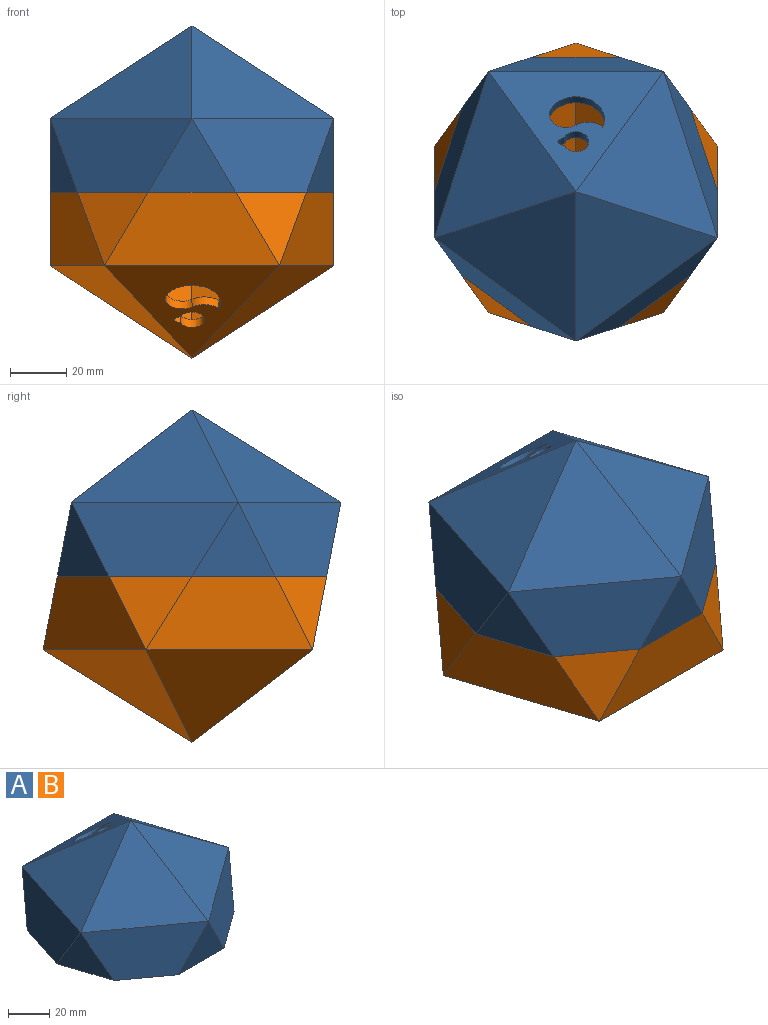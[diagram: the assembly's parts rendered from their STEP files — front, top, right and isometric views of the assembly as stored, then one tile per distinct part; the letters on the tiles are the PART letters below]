
ASSEMBLY  parts=2 mates=1
PART A: 43 faces, bbox 101.1x101.2x59.3 mm
  f0: plane 57.87x24.45mm, normal (0,-0.98,-0.19), area 1027.3mm2, adj f2,f20,f21,f26,f34,f35,f36
  f1: plane 28.74x24.45mm, normal (0,0.98,0.19), area 302.3mm2, adj f2,f24,f25,f31,f32,f33
  f2: plane 101.13x96.18mm, normal (0,0,-1), area 1072.3mm2, adj f0,f1,f3,f4,f5,f6,f7,f8
  f3: plane 29.53x26.42mm, normal (-0.93,-0.3,-0.19), area 417.6mm2, adj f2,f4,f12
  f4: plane 59.44x26.42mm, normal (-0.93,0.3,0.19), area 1263.3mm2, adj f2,f3,f5,f14
  f5: plane 26.42x25.12mm, normal (-0.58,0.79,-0.19), area 417.6mm2, adj f2,f4,f6
  f6: plane 62.5x26.42mm, normal (0,0.98,0.19), area 1263.3mm2, adj f2,f5,f7,f13
  f7: plane 26.42x25.12mm, normal (0.58,0.79,-0.19), area 417.6mm2, adj f2,f6,f8
  f8: plane 59.44x26.42mm, normal (0.93,0.3,0.19), area 1263.3mm2, adj f2,f7,f9,f15
  f9: plane 29.53x26.42mm, normal (0.93,-0.3,-0.19), area 417.6mm2, adj f2,f8,f10
  f10: plane 50.56x36.74mm, normal (0.58,-0.79,0.19), area 1263.3mm2, adj f2,f9,f11,f16
  f11: plane 31.05x26.42mm, normal (0,-0.98,-0.19), area 417.6mm2, adj f2,f10,f12
  f12: plane 50.56x36.74mm, normal (-0.58,-0.79,0.19), area 1263.3mm2, adj f2,f3,f11,f17
  f13: plane 62.5x43.01mm, normal (0,0.61,0.79), area 1417.1mm2, adj f6,f14,f15,f37,f38,f39,f40,f41
  f14: plane 59.44x50.56mm, normal (-0.58,0.19,0.79), area 1691.5mm2, adj f4,f13,f17
  f15: plane 59.44x50.56mm, normal (0.58,0.19,0.79), area 1691.5mm2, adj f8,f13,f16
  f16: plane 53.17x50.56mm, normal (0.36,-0.49,0.79), area 1691.5mm2, adj f10,f15,f17
  f17: plane 53.17x50.56mm, normal (-0.36,-0.49,0.79), area 1691.5mm2, adj f12,f14,f16
  f18: plane 27.33x24.45mm, normal (0.93,0.3,0.19), area 357.6mm2, adj f2,f19,f25
  f19: plane 55.04x24.45mm, normal (0.93,-0.3,-0.19), area 1082.6mm2, adj f2,f18,f20,f27
  f20: plane 24.45x23.25mm, normal (0.58,-0.79,0.19), area 357.6mm2, adj f0,f2,f19
  f21: plane 24.45x23.25mm, normal (-0.58,-0.79,0.19), area 357.6mm2, adj f0,f2,f22
  f22: plane 55.04x24.45mm, normal (-0.93,-0.3,-0.19), area 1082.6mm2, adj f2,f21,f23,f28
  f23: plane 27.33x24.45mm, normal (-0.93,0.3,0.19), area 357.6mm2, adj f2,f22,f24
  f24: plane 46.82x34.01mm, normal (-0.58,0.79,-0.19), area 1082.6mm2, adj f1,f2,f23,f29
  f25: plane 46.82x34.01mm, normal (0.58,0.79,-0.19), area 1082.6mm2, adj f1,f2,f18,f30
  f26: plane 57.87x39.83mm, normal (0,-0.61,-0.79), area 1175.7mm2, adj f0,f27,f28,f37,f38,f39,f40,f41
  f27: plane 55.04x46.82mm, normal (0.58,-0.19,-0.79), area 1450.1mm2, adj f19,f26,f30
  f28: plane 55.04x46.82mm, normal (-0.58,-0.19,-0.79), area 1450.1mm2, adj f22,f26,f29
  f29: plane 49.23x46.82mm, normal (-0.36,0.49,-0.79), area 1450.1mm2, adj f24,f28,f30
  f30: plane 49.23x46.82mm, normal (0.36,0.49,-0.79), area 1450.1mm2, adj f25,f27,f29
  f31: cylinder r=1.75mm len=17.5mm, axis (1,0,0), area 69.1mm2, adj f1,f32,f33
  f32: plane 3.11x1.31mm, normal (1,0,0), area 2.3mm2, adj f1,f31
  f33: plane 3.11x1.31mm, normal (-1,0,0), area 2.3mm2, adj f1,f31
  f34: cylinder r=1.75mm len=17.5mm, axis (1,0,0), area 69.1mm2, adj f0,f35,f36
  f35: plane 3.11x1.31mm, normal (1,0,0), area 2.3mm2, adj f0,f34
  f36: plane 3.11x1.31mm, normal (-1,0,0), area 2.3mm2, adj f0,f34
  f37: cylinder r=3.3mm len=3.84mm, axis (0,0.61,0.79), area 10.9mm2, adj f13,f26,f38,f39
  f38: cylinder r=4.5mm len=9.28mm, axis (0,0.61,0.79), area 86.4mm2, adj f13,f26,f37,f39
  f39: cylinder r=3.3mm len=3.84mm, axis (0,0.61,0.79), area 10.9mm2, adj f13,f26,f37,f38
  f40: cylinder r=10.23mm len=18.69mm, axis (0,0.61,0.79), area 103.6mm2, adj f13,f26,f41,f42
  f41: cylinder r=6mm len=9.57mm, axis (0,0.61,0.79), area 58.6mm2, adj f13,f26,f40,f42
  f42: cylinder r=7.27mm len=9.61mm, axis (0,0.61,0.79), area 37mm2, adj f13,f26,f40,f41
PART B: same geometry as A
PLACE A t=(-20.71,23.29,-5.87)mm
PLACE B rot(axis=(1,0,0),180deg) t=(-20.71,23.29,47.63)mm
MATE fastened B.f2 <-> A.f2  axis (0,0,1) through (-20.71,23.29,20.88)mm
